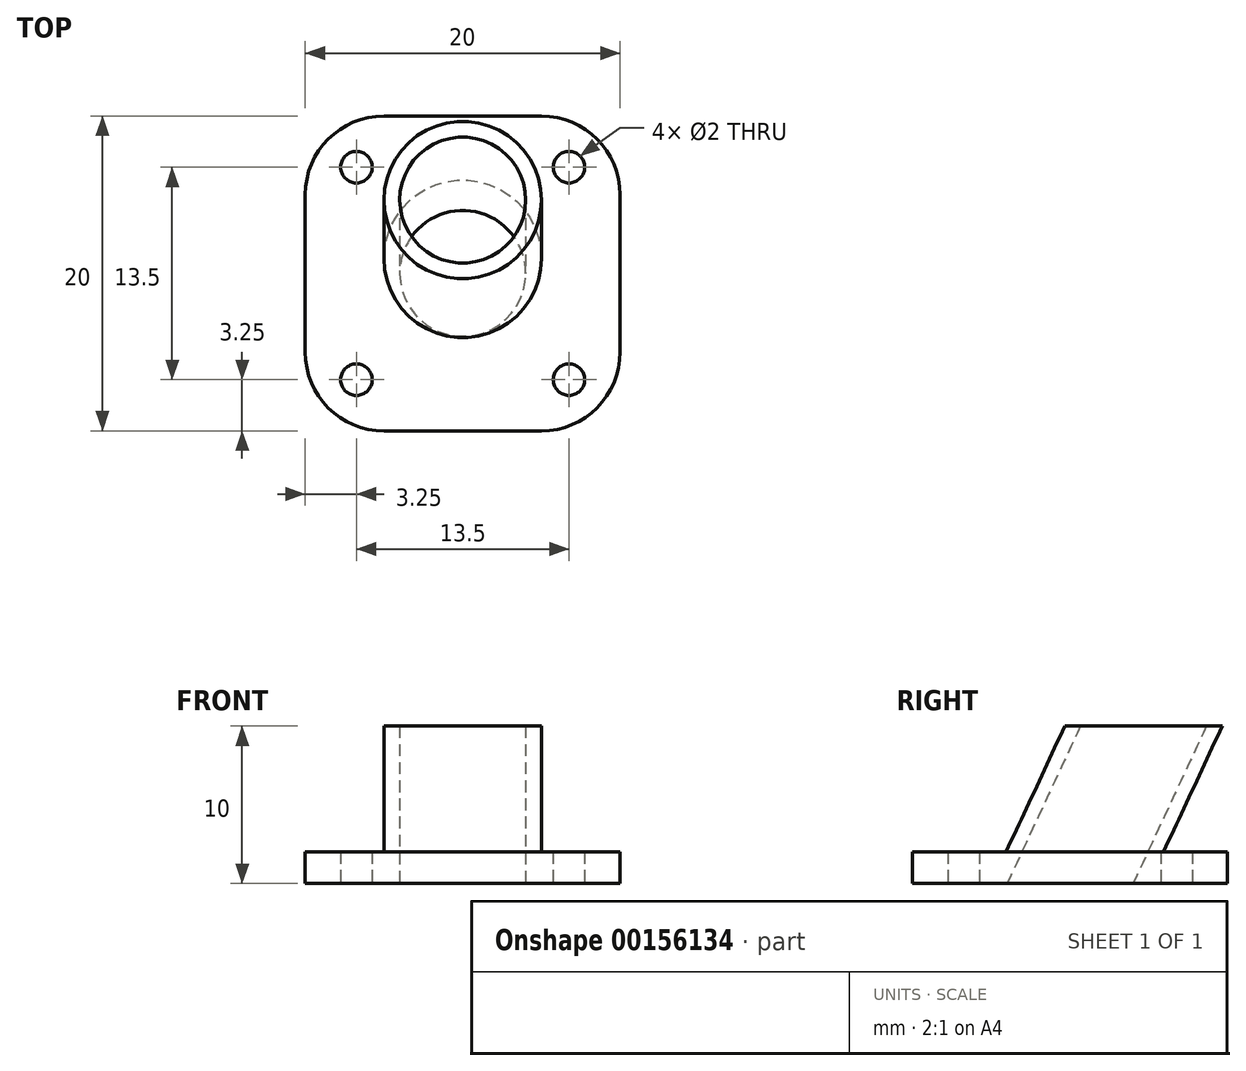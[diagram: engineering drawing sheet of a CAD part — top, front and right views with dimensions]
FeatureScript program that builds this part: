
annotation { "Feature Type Name" : "Feature", "Feature Type Description" : "" }
export const myFeature = defineFeature(function(context is Context, id is Id, definition is map)
    precondition{}
    {
        {
            var Q0;
            Q0=qCreatedBy(makeId("Top.planeOp"),FACE);
            var sketch = newSketch(context, id + "F0", { "sketchPlane" : qUnion([Q0])});
            skLineSegment(sketch, "E0.bottom", {"start": v(-5, 10) * mm, "end": v(5, 10) * mm});
            skLineSegment(sketch, "E0.top", {"start": v(-5, -10) * mm, "end": v(5, -10) * mm});
            skLineSegment(sketch, "E0.left", {"start": v(-10, 5) * mm, "end": v(-10, -5) * mm});
            skLineSegment(sketch, "E0.right", {"start": v(10, 5) * mm, "end": v(10, -5) * mm});
            skPoint(sketch, "E0.middle", {"position": v(0, 0) * mm});
            skCircle(sketch, "E1", {"center": v(0, 0) * mm, "radius": 4 * mm});
            skCircle(sketch, "E2", {"center": v(0, 0) * mm, "radius": 5 * mm});
            skCircle(sketch, "E3", {"center": v(-6.75, 6.75) * mm, "radius": 1 * mm});
            skCircle(sketch, "E4", {"center": v(6.75, 6.75) * mm, "radius": 1 * mm});
            skCircle(sketch, "E5", {"center": v(6.75, -6.75) * mm, "radius": 1 * mm});
            skCircle(sketch, "E6", {"center": v(-6.75, -6.75) * mm, "radius": 1 * mm});
            skPoint(sketch, "E7.visualSharp", {"position": v(-10, -10) * mm});
            skArc(sketch, "E7.filletArc", {"start": v(-10, -5) * mm, "mid": v(-8.54, -8.54) * mm, "end": v(-5, -10) * mm});
            skPoint(sketch, "E8.visualSharp", {"position": v(10, -10) * mm});
            skArc(sketch, "E8.filletArc", {"start": v(5, -10) * mm, "mid": v(8.54, -8.54) * mm, "end": v(10, -5) * mm});
            skPoint(sketch, "E9.visualSharp", {"position": v(10, 10) * mm});
            skArc(sketch, "E9.filletArc", {"start": v(10, 5) * mm, "mid": v(8.54, 8.54) * mm, "end": v(5, 10) * mm});
            skPoint(sketch, "E10.visualSharp", {"position": v(-10, 10) * mm});
            skArc(sketch, "E10.filletArc", {"start": v(-5, 10) * mm, "mid": v(-8.54, 8.54) * mm, "end": v(-10, 5) * mm});
            skSolve(sketch);
        }
        {
            var Q0;
            Q0 = qSketchRegion(id + "F0", true);
            var Q1;
            Q1=makeQuery(id+"F0.imprint","IMPRINT",FACE,{"disambiguationData":[TD([[makeQuery(id+"F0.imprint","IMPRINT",EDGE,{"derivedFrom":sQuery(id+"F0.wireOp",EDGE,"E1")}),-1.0]])]});
            var Q2;
            Q2=makeQuery(id+"F0.imprint","IMPRINT",FACE,{"disambiguationData":[TD([[makeQuery(id+"F0.imprint","IMPRINT",EDGE,{"derivedFrom":sQuery(id+"F0.wireOp",EDGE,"E1")}),1.0]])]});
            extrude(context, id + "F1", {"entities" : qUnion([Q0, Q1, Q2]), "depth" : 2 * mm});
        }
        {
            var Q0;
            Q0=qCreatedBy(makeId("Right.planeOp"),FACE);
            var sketch = newSketch(context, id + "F2", { "sketchPlane" : qUnion([Q0])});
            skLineSegment(sketch, "E11.0", {"start": v(-4, 0) * mm, "end": v(4, 0) * mm});
            skLineSegment(sketch, "E11.1", {"start": v(-5, 0) * mm, "end": v(5, 0) * mm});
            skLineSegment(sketch, "E12", {"start": v(4, 0) * mm, "end": v(8.66, 10) * mm});
            skLineSegment(sketch, "E13.0", {"start": v(5.75, 2) * mm, "end": v(7.75, 2) * mm});
            skSolve(sketch);
        }
        {
            var Q0;
            Q0=makeQuery(id+"F0.imprint","IMPRINT",FACE,{"disambiguationData":[TD([[makeQuery(id+"F0.imprint","IMPRINT",EDGE,{"derivedFrom":sQuery(id+"F0.wireOp",EDGE,"E1")}),-1.0]])]});
            var Q1;
            Q1=makeQuery(id+"F0.imprint","IMPRINT",FACE,{"disambiguationData":[TD([[makeQuery(id+"F0.imprint","IMPRINT",EDGE,{"derivedFrom":sQuery(id+"F0.wireOp",EDGE,"E1")}),1.0]])]});
            var Q2;
            Q2=sQuery(id+"F2.wireOp",EDGE,"E12");
            sweep(context, id + "F3", {"operationType" : NewBodyOperationType.ADD, "profiles" : qUnion([Q0, Q1]), "path" : qUnion([Q2]), "keepProfileOrientation" : true});
        }
        {
            var Q0;
            Q0=makeQuery(id+"F0.imprint","IMPRINT",FACE,{"disambiguationData":[TD([[makeQuery(id+"F0.imprint","IMPRINT",EDGE,{"derivedFrom":sQuery(id+"F0.wireOp",EDGE,"E1")}),1.0]])]});
            var Q1;
            Q1=sQuery(id+"F2.wireOp",EDGE,"E12");
            sweep(context, id + "F4", {"operationType" : NewBodyOperationType.REMOVE, "profiles" : qUnion([Q0]), "path" : qUnion([Q1])});
        }
    });
